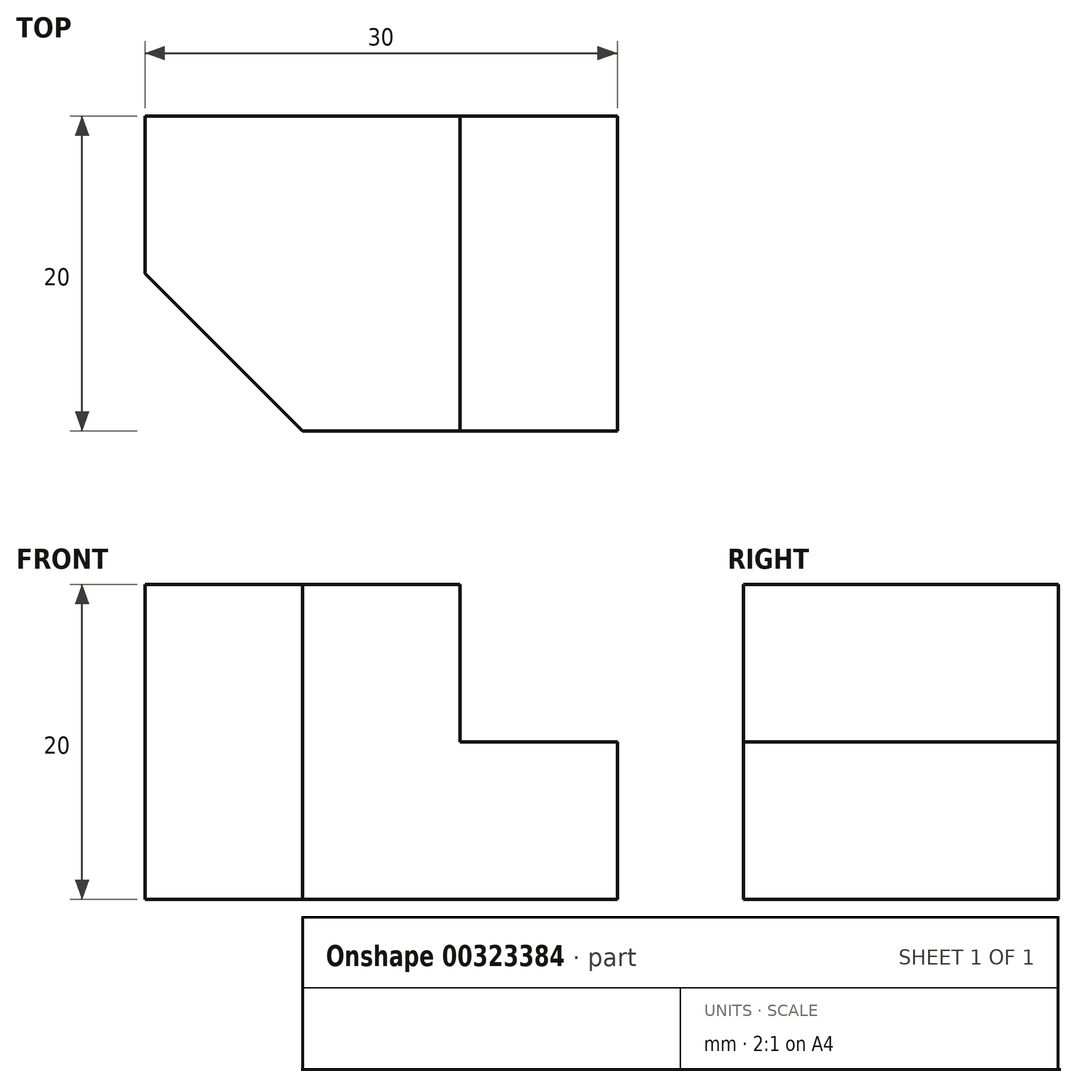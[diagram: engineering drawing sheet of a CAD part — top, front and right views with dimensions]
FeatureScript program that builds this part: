
annotation { "Feature Type Name" : "Feature", "Feature Type Description" : "" }
export const myFeature = defineFeature(function(context is Context, id is Id, definition is map)
    precondition{}
    {
        {
            var Q0;
            Q0=qCreatedBy(makeId("Top.planeOp"),FACE);
            var sketch = newSketch(context, id + "F0", { "sketchPlane" : qUnion([Q0])});
            skLineSegment(sketch, "E0", {"start": v(0, 0) * mm, "end": v(20, 0) * mm});
            skLineSegment(sketch, "E1", {"start": v(20, 0) * mm, "end": v(20, 20) * mm});
            skLineSegment(sketch, "E2", {"start": v(20, 20) * mm, "end": v(-10, 20) * mm});
            skLineSegment(sketch, "E3", {"start": v(-10, 20) * mm, "end": v(-10, 10) * mm});
            skLineSegment(sketch, "E4", {"start": v(-10, 10) * mm, "end": v(0, 0) * mm});
            skSolve(sketch);
        }
        {
            var Q0;
            Q0 = qSketchRegion(id + "F0", true);
            extrude(context, id + "F1", {"entities" : qUnion([Q0]), "endBound" : BoundingType.SYMMETRIC, "depth" : 20 * mm});
        }
        {
            var Q0;
            Q0=makeQuery(id+"F1.opExtrude","CAP_FACE",FACE,{"disambiguationData":[OSD([sQuery(id+"F0.wireOp",EDGE,"E0"),sQuery(id+"F0.wireOp",EDGE,"E1"),sQuery(id+"F0.wireOp",EDGE,"E2"),sQuery(id+"F0.wireOp",EDGE,"E3"),sQuery(id+"F0.wireOp",EDGE,"E4")])],"isStart":false});
            var sketch = newSketch(context, id + "F2", { "sketchPlane" : qUnion([Q0])});
            skLineSegment(sketch, "E5", {"start": v(20, 20) * mm, "end": v(10, 20) * mm});
            skLineSegment(sketch, "E6", {"start": v(10, 20) * mm, "end": v(10, 0) * mm});
            skLineSegment(sketch, "E7", {"start": v(10, 0) * mm, "end": v(20, 0) * mm});
            skLineSegment(sketch, "E8", {"start": v(20, 0) * mm, "end": v(20, 20) * mm});
            skSolve(sketch);
        }
        {
            var Q0;
            Q0 = qSketchRegion(id + "F2", true);
            extrude(context, id + "F3", {"entities" : qUnion([Q0]), "operationType" : NewBodyOperationType.REMOVE, "oppositeDirection" : true, "depth" : 10 * mm});
        }
    });
